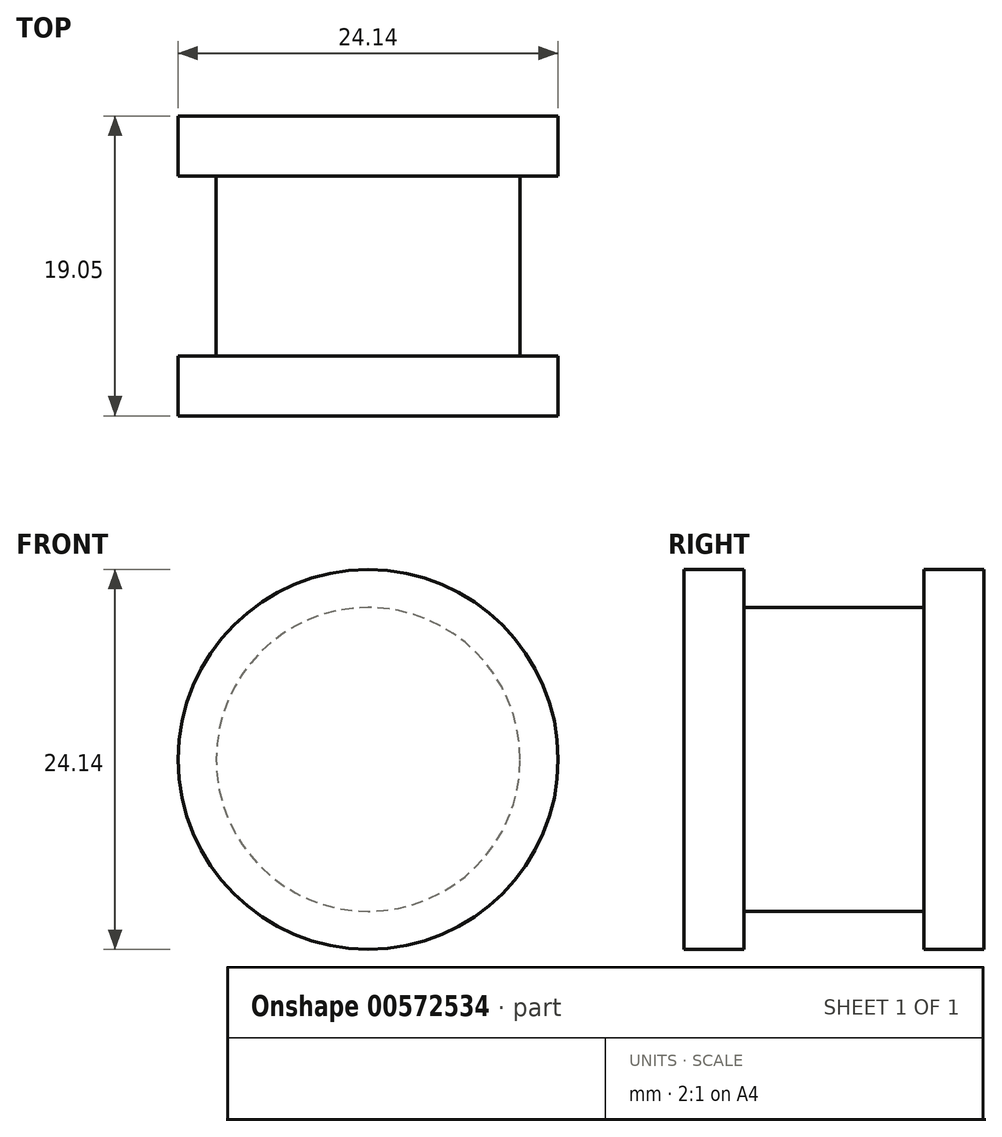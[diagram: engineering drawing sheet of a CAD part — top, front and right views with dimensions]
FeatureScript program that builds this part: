
annotation { "Feature Type Name" : "Feature", "Feature Type Description" : "" }
export const myFeature = defineFeature(function(context is Context, id is Id, definition is map)
    precondition{}
    {
        {
            var Q0;
            Q0=qCreatedBy(makeId("Front.planeOp"),FACE);
            var sketch = newSketch(context, id + "F0", { "sketchPlane" : qUnion([Q0])});
            skCircle(sketch, "E0", {"center": v(0, 0) * mm, "radius": 12.07 * mm});
            skSolve(sketch);
        }
        {
            var Q0;
            Q0=makeQuery(id+"F0.imprint","IMPRINT",FACE,{"disambiguationData":[TD([[makeQuery(id+"F0.imprint","IMPRINT",EDGE,{"derivedFrom":sQuery(id+"F0.wireOp",EDGE,"E0")}),1.0]])]});
            extrude(context, id + "F1", {"entities" : qUnion([Q0]), "oppositeDirection" : true, "depth" : 3.8 * mm, "offsetDistance" : 25.4 * mm});
        }
        {
            var Q0;
            Q0=makeQuery(id+"F1.opExtrude","CAP_FACE",FACE,{"disambiguationData":[OSD([sQuery(id+"F0.wireOp",EDGE,"E0")])],"isStart":true});
            var sketch = newSketch(context, id + "F2", { "sketchPlane" : qUnion([Q0])});
            skCircle(sketch, "E1", {"center": v(0, 0) * mm, "radius": 9.65 * mm});
            skSolve(sketch);
        }
        {
            var Q0;
            Q0=makeQuery(id+"F2.imprint","IMPRINT",FACE,{"disambiguationData":[TD([[makeQuery(id+"F2.imprint","IMPRINT",EDGE,{"derivedFrom":sQuery(id+"F2.wireOp",EDGE,"E1")}),1.0]])]});
            extrude(context, id + "F3", {"entities" : qUnion([Q0]), "operationType" : NewBodyOperationType.ADD, "depth" : 11.43 * mm, "offsetDistance" : 25.4 * mm});
        }
        {
            var Q0;
            Q0=makeQuery(id+"F3.opExtrude","CAP_FACE",FACE,{"disambiguationData":[OSD([sQuery(id+"F2.wireOp",EDGE,"E1")])],"isStart":false});
            var sketch = newSketch(context, id + "F4", { "sketchPlane" : qUnion([Q0])});
            skCircle(sketch, "E2", {"center": v(0, 0) * mm, "radius": 12.07 * mm});
            skSolve(sketch);
        }
        {
            var Q0;
            Q0 = qSketchRegion(id + "F4", true);
            extrude(context, id + "F5", {"entities" : qUnion([Q0]), "operationType" : NewBodyOperationType.ADD, "depth" : 3.8 * mm, "offsetDistance" : 25.4 * mm});
        }
    });
